FCSTD DOCUMENT  (FreeCAD 0.14R3702 (Git))
Label: horloge
License: CC-BY 3.0
LicenseURL: http://creativecommons.org/licenses/by/3.0/
objects: Sketcher::SketchObject×1
note: 1 computed .brp shape members not serialized (recipe doc carries the construction recipe); baked Part::Feature solids carry a one-line shape summary decoded from their .brp

FEATURE [Sketcher::SketchObject] Sketch
  Placement = pos=(0,0,0) rot=(-1,0,0;4.71239rad)
  sketch-geometry (4):
    g0: Circle CenterX=0 CenterY=0 CenterZ=0 NormalX=0 NormalY=0 NormalZ=1 Radius=150
    g1: ArcOfCircle CenterX=-89.3029 CenterY=55 CenterZ=0 NormalX=0 NormalY=0 NormalZ=1 Radius=100 StartAngle=5.81642 EndAngle=6.74995
    g2: Circle CenterX=0 CenterY=0 CenterZ=0 NormalX=0 NormalY=0 NormalZ=1 Radius=100
    g3: ArcOfCircle CenterX=89.3029 CenterY=55 CenterZ=0 NormalX=0 NormalY=0 NormalZ=1 Radius=100 StartAngle=2.67483 EndAngle=3.60836
  constraints (12):
    c: Coincident(g-1,g0)
    c: Radius(g0) = 150
    c: Radius(g2) = 100
    c: Coincident(g2,g-1)
    c: DistanceX(g1) = 0
    c: DistanceY(g-1,g1) = 10
    c: DistanceY(g-1,g1) = 100
    c: Radius(g1) = 100
    c: DistanceX(g-1,g1) = 0
    c: Coincident(g3,g1)
    c: Coincident(g3,g1)
    c: Radius(g3) = 100
